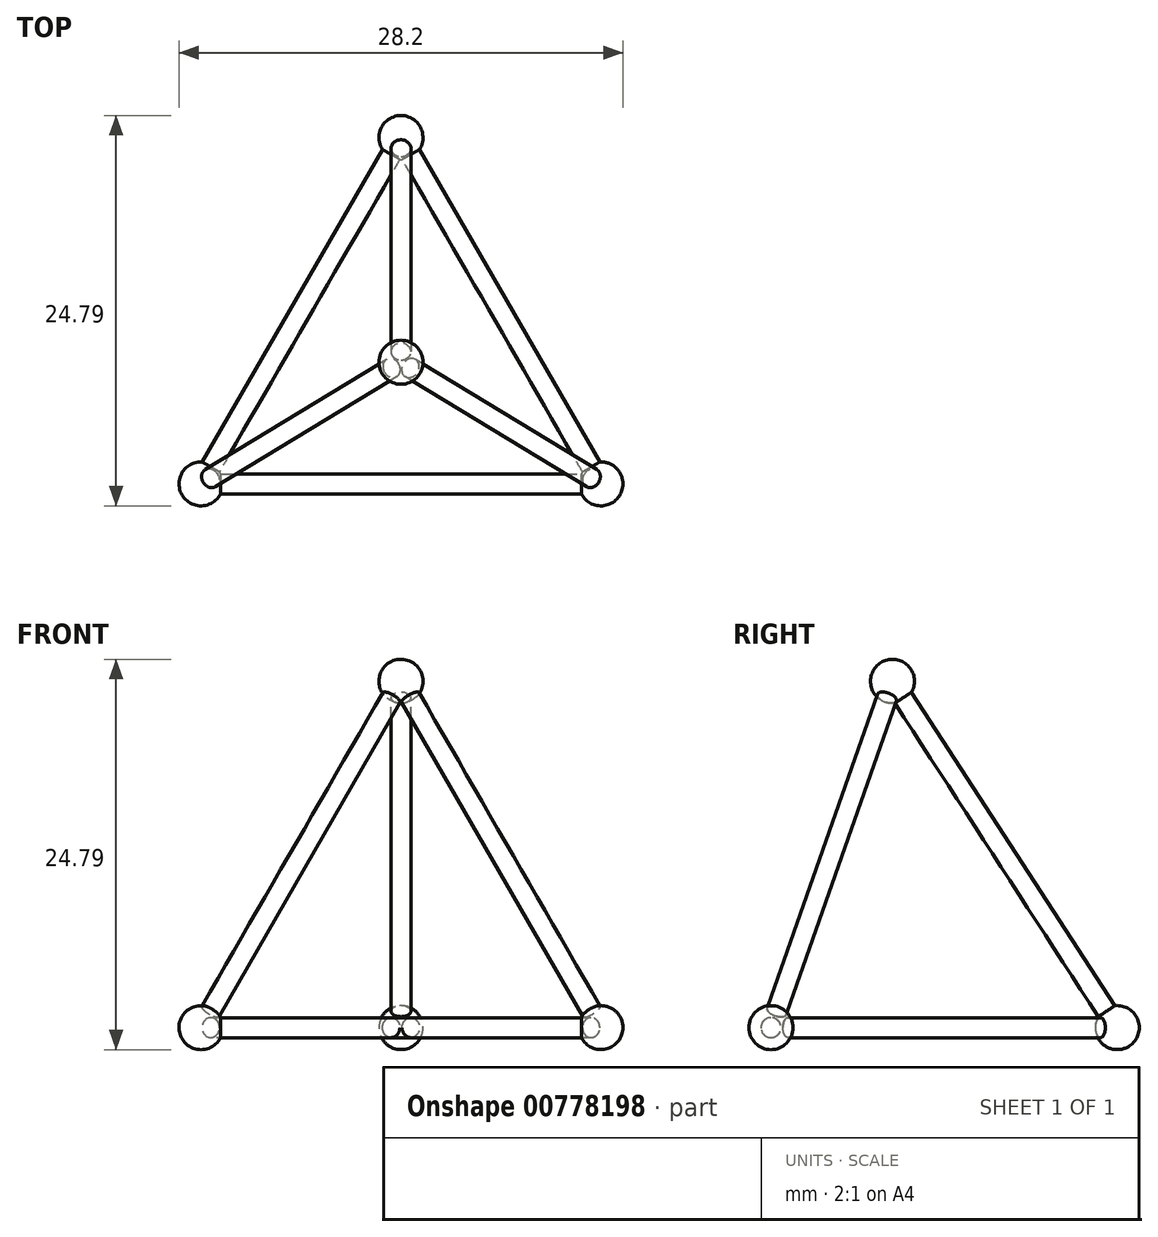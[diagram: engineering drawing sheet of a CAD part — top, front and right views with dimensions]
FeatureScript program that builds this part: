
annotation { "Feature Type Name" : "Feature", "Feature Type Description" : "" }
export const myFeature = defineFeature(function(context is Context, id is Id, definition is map)
    precondition{}
    {
        {
            var Q0;
            Q0=qCreatedBy(makeId("Top.planeOp"),FACE);
            var sketch = newSketch(context, id + "F0", { "sketchPlane" : qUnion([Q0])});
            skLineSegment(sketch, "E0", {"start": v(0, 14.28) * mm, "end": v(12.7, -7.72) * mm});
            skLineSegment(sketch, "E1", {"start": v(0, 14.28) * mm, "end": v(-12.7, -7.72) * mm});
            skLineSegment(sketch, "E2", {"start": v(-12.7, -7.72) * mm, "end": v(12.7, -7.72) * mm});
            skLineSegment(sketch, "E3", {"start": v(0, 0) * mm, "end": v(14.32, 8.27) * mm, "construction": true});
            skLineSegment(sketch, "E4", {"start": v(0, 0) * mm, "end": v(-6.18, 3.57) * mm, "construction": true});
            skSolve(sketch);
        }
        {
            var Q0;
            Q0=qCreatedBy(makeId("Right.planeOp"),FACE);
            var sketch = newSketch(context, id + "F1", { "sketchPlane" : qUnion([Q0])});
            skLineSegment(sketch, "E5", {"start": v(0, 0) * mm, "end": v(0, 22) * mm, "construction": true});
            skLineSegment(sketch, "E6", {"start": v(0, 22) * mm, "end": v(0, 0) * mm, "construction": true});
            skSolve(sketch);
        }
        {
            var Q0;
            Q0=sQuery(id+"F0.wireOp",VERTEX,"E0.end");
            var Q1;
            Q1=sQuery(id+"F0.wireOp",VERTEX,"E1.end");
            var Q2;
            Q2=sQuery(id+"F1.wireOp",VERTEX,"E5.end");
            cPlane(context, id + "F2", {"entities" : qUnion([Q0, Q1, Q2]), "cplaneType" : CPlaneType.THREE_POINT, "offset" : 25.4 * mm, "width" : 152.4 * mm, "height" : 152.4 * mm});
        }
        {
            var Q0;
            Q0=sQuery(id+"F0.wireOp",VERTEX,"E0.end");
            var Q1;
            Q1=sQuery(id+"F0.wireOp",VERTEX,"E0.start");
            var Q2;
            Q2=sQuery(id+"F1.wireOp",VERTEX,"E5.end");
            cPlane(context, id + "F3", {"entities" : qUnion([Q0, Q1, Q2]), "cplaneType" : CPlaneType.THREE_POINT, "offset" : 25.4 * mm, "width" : 152.4 * mm, "height" : 152.4 * mm});
        }
        {
            var Q0;
            Q0=sQuery(id+"F0.wireOp",VERTEX,"E0.start");
            var Q1;
            Q1=sQuery(id+"F0.wireOp",VERTEX,"E1.end");
            var Q2;
            Q2=sQuery(id+"F1.wireOp",VERTEX,"E5.end");
            cPlane(context, id + "F4", {"entities" : qUnion([Q0, Q1, Q2]), "cplaneType" : CPlaneType.THREE_POINT, "offset" : 25.4 * mm, "width" : 152.4 * mm, "height" : 152.4 * mm});
        }
        {
            var Q0;
            Q0=qCreatedBy(id+"F2.planeOp",FACE);
            var sketch = newSketch(context, id + "F5", { "sketchPlane" : qUnion([Q0])});
            skLineSegment(sketch, "E7", {"start": v(-12.7, -2.56) * mm, "end": v(0, 20.76) * mm});
            skLineSegment(sketch, "E8", {"start": v(-12.7, -2.56) * mm, "end": v(12.7, -2.56) * mm});
            skLineSegment(sketch, "E9", {"start": v(12.7, -2.56) * mm, "end": v(0, 20.76) * mm});
            skSolve(sketch);
        }
        {
            var Q0;
            Q0=qCreatedBy(id+"F3.planeOp",FACE);
            var sketch = newSketch(context, id + "F6", { "sketchPlane" : qUnion([Q0])});
            skLineSegment(sketch, "E10", {"start": v(3.67, 20.6) * mm, "end": v(12.45, -4.46) * mm});
            skLineSegment(sketch, "E11", {"start": v(12.45, -4.46) * mm, "end": v(-12.56, 0) * mm});
            skLineSegment(sketch, "E12", {"start": v(-12.56, 0) * mm, "end": v(3.67, 20.6) * mm});
            skLineSegment(sketch, "E13", {"start": v(12.45, -4.46) * mm, "end": v(-4.44, 10.3) * mm, "construction": true});
            skSolve(sketch);
        }
        {
            var Q0;
            Q0=qCreatedBy(id+"F4.planeOp",FACE);
            var sketch = newSketch(context, id + "F7", { "sketchPlane" : qUnion([Q0])});
            skLineSegment(sketch, "E14", {"start": v(-3.67, 20.6) * mm, "end": v(12.56, 0) * mm});
            skLineSegment(sketch, "E15", {"start": v(12.56, 0) * mm, "end": v(-12.45, -4.46) * mm});
            skLineSegment(sketch, "E16", {"start": v(-12.45, -4.46) * mm, "end": v(-3.67, 20.6) * mm});
            skSolve(sketch);
        }
        {
            var Q0;
            Q0=qCreatedBy(makeId("Right.planeOp"),FACE);
            var sketch = newSketch(context, id + "F8", { "sketchPlane" : qUnion([Q0])});
            skCircle(sketch, "E17", {"center": v(-7.72, 0) * mm, "radius": 0.64 * mm});
            skSolve(sketch);
        }
        {
            var Q0;
            Q0=makeQuery(id+"F8.imprint","IMPRINT",FACE,{"disambiguationData":[TD([[makeQuery(id+"F8.imprint","IMPRINT",EDGE,{"derivedFrom":sQuery(id+"F8.wireOp",EDGE,"E17")}),1.0]])]});
            var Q1;
            Q1=sQuery(id+"F5.wireOp",EDGE,"E8");
            var Q2;
            Q2=sQuery(id+"F6.wireOp",EDGE,"E11");
            var Q3;
            Q3=sQuery(id+"F0.wireOp",EDGE,"E1");
            sweep(context, id + "F9", {"profiles" : qUnion([Q0]), "path" : qUnion([Q1, Q2, Q3])});
        }
        {
            var Q0;
            Q0=sQuery(id+"F7.wireOp",EDGE,"E14");
            cPoint(context, id + "F10", {"entities" : qUnion([Q0]), "parameter" : 0.5});
        }
        {
            var Q0;
            Q0 = qCreatedBy(id + "F10" ,VERTEX);
            var Q1;
            Q1=sQuery(id+"F0.wireOp",VERTEX,"E1.end");
            var Q2;
            Q2=sQuery(id+"F0.wireOp",VERTEX,"E0.end");
            cPlane(context, id + "F11", {"entities" : qUnion([Q0, Q1, Q2]), "cplaneType" : CPlaneType.THREE_POINT, "offset" : 25.4 * mm, "width" : 152.4 * mm, "height" : 152.4 * mm});
        }
        {
            var Q0;
            Q0=qCreatedBy(id+"F11.planeOp",FACE);
            var sketch = newSketch(context, id + "F12", { "sketchPlane" : qUnion([Q0])});
            skCircle(sketch, "E18", {"center": v(0, -12.28) * mm, "radius": 0.64 * mm});
            skSolve(sketch);
        }
        {
            var Q0;
            Q0 = qSketchRegion(id + "F8", true);
            var Q1;
            Q1=sQuery(id+"F7.wireOp",EDGE,"E16");
            var Q2;
            Q2=sQuery(id+"F5.wireOp",EDGE,"E9");
            var Q3;
            Q3=sQuery(id+"F5.wireOp",EDGE,"E8");
            sweep(context, id + "F13", {"operationType" : NewBodyOperationType.ADD, "profiles" : qUnion([Q0]), "path" : qUnion([Q1, Q2, Q3])});
        }
        {
            var Q0;
            Q0=makeQuery(id+"F12.imprint","IMPRINT",FACE,{"disambiguationData":[TD([[makeQuery(id+"F12.imprint","IMPRINT",EDGE,{"derivedFrom":sQuery(id+"F12.wireOp",EDGE,"E18")}),1.0]])]});
            var Q1;
            Q1=sQuery(id+"F7.wireOp",EDGE,"E14");
            var Q2;
            Q2=sQuery(id+"F6.wireOp",EDGE,"E11");
            var Q3;
            Q3=sQuery(id+"F5.wireOp",EDGE,"E9");
            sweep(context, id + "F14", {"operationType" : NewBodyOperationType.ADD, "profiles" : qUnion([Q0]), "path" : qUnion([Q1, Q2, Q3])});
        }
        {
            var Q0;
            Q0=qCreatedBy(id+"F4.planeOp",FACE);
            var sketch = newSketch(context, id + "F15", { "sketchPlane" : qUnion([Q0])});
            skArc(sketch, "E19", {"start": v(13.96, 0) * mm, "mid": v(12.56, 1.4) * mm, "end": v(11.16, 0) * mm});
            skLineSegment(sketch, "E20", {"start": v(12.56, 0) * mm, "end": v(13.96, 0) * mm});
            skLineSegment(sketch, "E21", {"start": v(12.56, 0) * mm, "end": v(11.16, 0) * mm});
            skSolve(sketch);
        }
        {
            var Q0;
            Q0 = qSketchRegion(id + "F15", true);
            var Q1;
            Q1=sQuery(id+"F15.wireOp",EDGE,"E21");
            revolve(context, id + "F16", {"operationType" : NewBodyOperationType.ADD, "surfaceOperationType" : NewSurfaceOperationType.NEW, "entities" : qUnion([Q0]), "axis" : qUnion([Q1]), "revolveType" : RevolveType.FULL});
        }
        {
            var Q0;
            Q0=qCreatedBy(id+"F4.planeOp",FACE);
            var sketch = newSketch(context, id + "F17", { "sketchPlane" : qUnion([Q0])});
            skArc(sketch, "E22", {"start": v(-11.05, -4.46) * mm, "mid": v(-12.45, -3.06) * mm, "end": v(-13.84, -4.46) * mm});
            skLineSegment(sketch, "E23", {"start": v(-13.84, -4.46) * mm, "end": v(-11.05, -4.46) * mm});
            skSolve(sketch);
        }
        {
            var Q0;
            Q0=makeQuery(id+"F17.imprint","IMPRINT",FACE,{"disambiguationData":[TD([[makeQuery(id+"F17.imprint","IMPRINT",EDGE,{"derivedFrom":sQuery(id+"F17.wireOp",EDGE,"E22")}),1.0]])]});
            var Q1;
            Q1=sQuery(id+"F17.wireOp",EDGE,"E23");
            revolve(context, id + "F18", {"operationType" : NewBodyOperationType.ADD, "surfaceOperationType" : NewSurfaceOperationType.NEW, "entities" : qUnion([Q0]), "axis" : qUnion([Q1]), "revolveType" : RevolveType.FULL});
        }
        {
            var Q0;
            Q0=qCreatedBy(id+"F4.planeOp",FACE);
            var sketch = newSketch(context, id + "F19", { "sketchPlane" : qUnion([Q0])});
            skArc(sketch, "E24", {"start": v(-5.07, 20.6) * mm, "mid": v(-3.67, 19.2) * mm, "end": v(-2.27, 20.6) * mm});
            skLineSegment(sketch, "E25", {"start": v(-3.67, 20.6) * mm, "end": v(-5.07, 20.6) * mm});
            skLineSegment(sketch, "E26", {"start": v(-3.67, 20.6) * mm, "end": v(-2.27, 20.6) * mm});
            skSolve(sketch);
        }
        {
            var Q0;
            Q0 = qSketchRegion(id + "F19", true);
            var Q1;
            Q1=sQuery(id+"F19.wireOp",EDGE,"E25");
            revolve(context, id + "F20", {"operationType" : NewBodyOperationType.ADD, "surfaceOperationType" : NewSurfaceOperationType.NEW, "entities" : qUnion([Q0]), "axis" : qUnion([Q1]), "revolveType" : RevolveType.FULL});
        }
        {
            var Q0;
            Q0=qCreatedBy(id+"F2.planeOp",FACE);
            var sketch = newSketch(context, id + "F21", { "sketchPlane" : qUnion([Q0])});
            skArc(sketch, "E27", {"start": v(14.1, -2.56) * mm, "mid": v(12.7, -1.16) * mm, "end": v(11.3, -2.56) * mm});
            skLineSegment(sketch, "E28", {"start": v(12.7, -2.56) * mm, "end": v(14.1, -2.56) * mm});
            skLineSegment(sketch, "E29", {"start": v(12.7, -2.56) * mm, "end": v(11.3, -2.56) * mm});
            skSolve(sketch);
        }
        {
            var Q0;
            Q0=makeQuery(id+"F21.imprint","IMPRINT",FACE,{"disambiguationData":[TD([[makeQuery(id+"F21.imprint","IMPRINT",EDGE,{"derivedFrom":sQuery(id+"F21.wireOp",EDGE,"E27")}),1.0]])]});
            var Q1;
            Q1=sQuery(id+"F21.wireOp",EDGE,"E29");
            revolve(context, id + "F22", {"operationType" : NewBodyOperationType.ADD, "surfaceOperationType" : NewSurfaceOperationType.NEW, "entities" : qUnion([Q0]), "axis" : qUnion([Q1]), "revolveType" : RevolveType.FULL});
        }
    });
